# Revit family: Sink-Double Centre Bowl-Clark Advance1
name_source: partatom
category: Plumbing Fixtures
revit_build: Autodesk Revit Architecture 2012 (Build: 20110916_2132(x64)
units: mm (PartAtom-declared; Revit-internal decimal feet)

## types (1)
- Advance Double Centre Bowl - 0TH
    1 Taphole = No
    3 Tapholes = No
    Assembly Code = D2010410
    CW Connection = No
    Cost = 0 $
    Default Elevation = 0 mm  [stored 0 ft]
    Depth_ANZRS = 174 mm  [stored 0.570866 ft]
    Description = Advance Double Centre Bowl
    HW Connection = No
    Keynote = SK
    Length_ANZRS = 1530 mm  [stored 5.01969 ft]
    Manufacturer = Clark
    Material_ANZRS = Metal-Stainless-Caroma
    Model = 3507
    Spout Penetation = 100 mm  [stored 0.328084 ft]
    Tap Penetations = 100 mm  [stored 0.328084 ft]
    Type Comments = Includes basket waste, Bowl Volume 20L per bowl, Carton size 1540 x 490 x 195, Carton weight 7kg, Match with Irwell Pin mixer range
    URL = http://www.clark.com.au
    Vent Connection = No
    WFU = 2
    Waste Connection = Yes
    Waste Radius = 30 mm  [stored 0.0984252 ft]
    Width_ANZRS = 480 mm  [stored 1.5748 ft]

note: [stored X ft] marks values corroborated as IEEE doubles in the binary element streams (Revit-internal decimal feet)

## geometry (parser evidence)
native form markers: Blend x6, Sweep x2
no freeform markers — native parametric forms only
